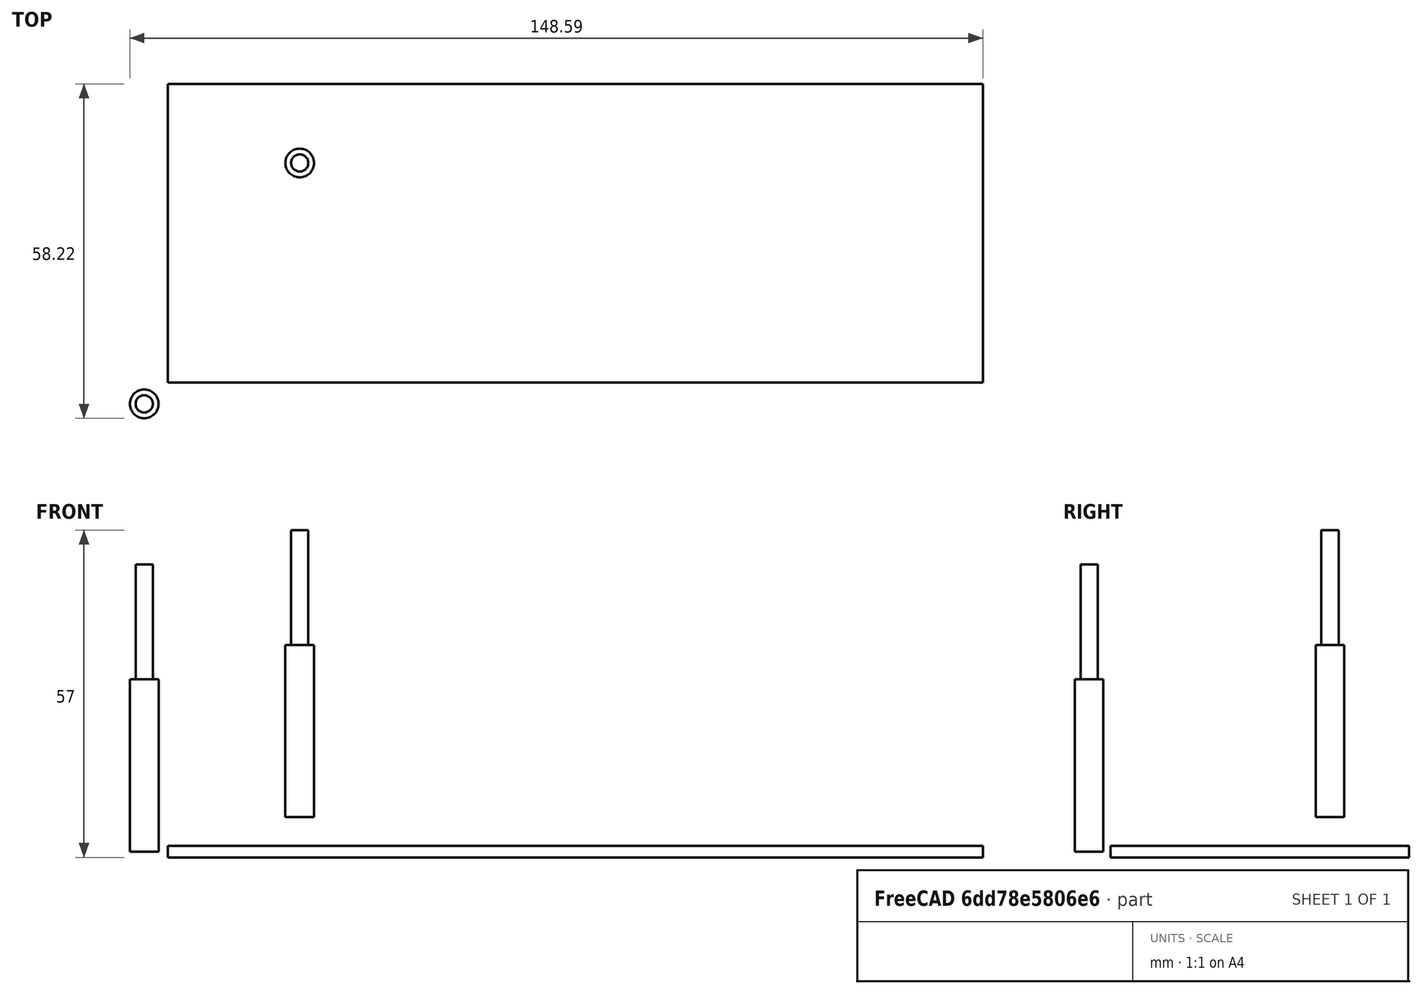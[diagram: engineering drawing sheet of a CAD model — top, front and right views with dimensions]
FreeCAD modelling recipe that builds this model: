
FCSTD DOCUMENT  (FreeCAD 1.0R39109 (Git))
Label: Sensors
License: All rights reserved
LicenseURL: https://en.wikipedia.org/wiki/All_rights_reserved
objects: Sketcher::SketchObject×6, App::DocumentObjectGroup×3, Part::FeaturePython×3, Path::FeaturePython×3, PartDesign::Body×1, App::FeaturePython×1, Part::Part2DObjectPython×1, Mesh::FeaturePython×1
note: 17 computed .brp shape members not serialized (recipe doc carries the construction recipe); baked Part::Feature solids carry a one-line shape summary decoded from their .brp

FEATURE [Sketcher::SketchObject] Sketch004
  ArcFitTolerance = 1e-06
  AttachmentSupport = -> [XY_Plane]
  FullyConstrained = false
  MakeInternals = false
  MapMode = 5
  sketch-geometry (28):
    g0: LineSegment StartX=5.18436 StartY=54.9008 StartZ=0 EndX=5.18436 EndY=4.90076 EndZ=0
    g1: LineSegment StartX=5.18436 StartY=4.90076 StartZ=0 EndX=145.184 EndY=4.90076 EndZ=0
    g2: LineSegment StartX=145.184 StartY=54.9008 StartZ=0 EndX=5.18436 EndY=54.9008 EndZ=0
    g3: LineSegment StartX=145.184 StartY=4.90076 StartZ=0 EndX=145.184 EndY=29.9008 EndZ=0
    g4: LineSegment StartX=145.184 StartY=29.9008 StartZ=0 EndX=145.184 EndY=54.9008 EndZ=0
    g5: LineSegment [constr] StartX=145.184 StartY=29.9008 StartZ=0 EndX=5.18436 EndY=29.9008 EndZ=0
    g6: LineSegment StartX=128.684 StartY=29.9008 StartZ=0 EndX=128.684 EndY=37.4008 EndZ=0
    g7: LineSegment StartX=128.684 StartY=37.4008 StartZ=0 EndX=121.684 EndY=37.4008 EndZ=0
    g8: LineSegment StartX=121.684 StartY=37.4008 StartZ=0 EndX=121.684 EndY=22.4008 EndZ=0
    g9: LineSegment StartX=128.684 StartY=22.4008 StartZ=0 EndX=128.684 EndY=29.9008 EndZ=0
    g10: LineSegment StartX=121.684 StartY=22.4008 StartZ=0 EndX=125.184 EndY=22.4008 EndZ=0
    g11: LineSegment StartX=125.184 StartY=22.4008 StartZ=0 EndX=128.684 EndY=22.4008 EndZ=0
    g12: LineSegment [constr] StartX=125.184 StartY=40.4008 StartZ=0 EndX=125.184 EndY=29.9008 EndZ=0
    g13: LineSegment [constr] StartX=125.184 StartY=29.9008 StartZ=0 EndX=125.184 EndY=19.4008 EndZ=0
    g14: Circle CenterX=125.184 CenterY=19.4008 CenterZ=0 NormalX=0 NormalY=0 NormalZ=1 AngleXU=0 Radius=2
    g15: Circle CenterX=125.184 CenterY=40.4008 CenterZ=0 NormalX=0 NormalY=0 NormalZ=1 AngleXU=0 Radius=2
    g16: LineSegment StartX=28.6844 StartY=29.9008 StartZ=0 EndX=28.6844 EndY=37.4008 EndZ=0
    g17: LineSegment StartX=28.6844 StartY=37.4008 StartZ=0 EndX=21.6844 EndY=37.4008 EndZ=0
    g18: LineSegment StartX=21.6844 StartY=37.4008 StartZ=0 EndX=21.6844 EndY=22.4008 EndZ=0
    g19: LineSegment StartX=28.6844 StartY=22.4008 StartZ=0 EndX=28.6844 EndY=29.9008 EndZ=0
    g20: LineSegment StartX=21.6844 StartY=22.4008 StartZ=0 EndX=25.1844 EndY=22.4008 EndZ=0
    g21: LineSegment StartX=25.1844 StartY=22.4008 StartZ=0 EndX=28.6844 EndY=22.4008 EndZ=0
    g22: LineSegment [constr] StartX=25.1844 StartY=40.4008 StartZ=0 EndX=25.1844 EndY=29.9008 EndZ=0
    g23: LineSegment [constr] StartX=25.1844 StartY=29.9008 StartZ=0 EndX=25.1844 EndY=19.4008 EndZ=0
    g24: Circle CenterX=25.1844 CenterY=19.4008 CenterZ=0 NormalX=0 NormalY=0 NormalZ=1 AngleXU=0 Radius=2
    g25: Circle CenterX=25.1844 CenterY=40.4008 CenterZ=0 NormalX=0 NormalY=0 NormalZ=1 AngleXU=0 Radius=2
    g26: LineSegment [constr] StartX=25.1844 StartY=19.4008 StartZ=0 EndX=125.184 EndY=19.4008 EndZ=0
    g27: LineSegment [constr] StartX=25.1844 StartY=40.4008 StartZ=0 EndX=125.184 EndY=40.4008 EndZ=0
  constraints (78):
    c: Coincident(g0,g1)
    c: Coincident(g2,g0)
    c: Vertical(g0)
    c: Horizontal(g1)
    c: Horizontal(g2)
    c: DistanceX(g2,g2) = 140
    c: DistanceY(g1,g2) = 50
    c: Coincident(g3,g1)
    c: Vertical(g3)
    c: Coincident(g4,g3)
    c: Coincident(g4,g2)
    c: Vertical(g4)
    c: Equal(g3,g4)
    c: Coincident(g5,g3)
    c: PointOnObject(g5,g0)
    c: Horizontal(g5)
    c: PointOnObject(g6,g5)
    c: Vertical(g6)
    c: Coincident(g7,g6)
    c: Horizontal(g7)
    c: Coincident(g8,g7)
    c: Vertical(g8)
    c: Coincident(g9,g6)
    c: Vertical(g9)
    c: Equal(g9,g6)
    c: DistanceX(g7,g7) = 7
    c: DistanceY(g8,g8) = 15
    c: Coincident(g10,g8)
    c: Horizontal(g10)
    c: Coincident(g11,g10)
    c: Coincident(g11,g9)
    c: Horizontal(g11)
    c: Equal(g10,g11)
    c: PointOnObject(g12,g5)
    c: Vertical(g12)
    c: Coincident(g13,g12)
    c: Vertical(g13)
    c: PointOnObject(g10,g13)
    c: Equal(g12,g13)
    c: Coincident(g14,g13)
    c: Coincident(g15,g12)
    c: Diameter(g15) = 4
    c: Equal(g14,g15)
    c: Vertical(g16)
    c: Coincident(g17,g16)
    c: Horizontal(g17)
    c: Coincident(g18,g17)
    c: Vertical(g18)
    c: Coincident(g19,g16)
    c: Vertical(g19)
    c: Equal(g19,g16)
    c: DistanceX(g17,g17) = 7
    c: DistanceY(g18,g18) = 15
    c: Coincident(g20,g18)
    c: Horizontal(g20)
    c: Coincident(g21,g20)
    c: Coincident(g21,g19)
    c: Horizontal(g21)
    c: Equal(g20,g21)
    c: Vertical(g22)
    c: Coincident(g23,g22)
    c: Vertical(g23)
    c: PointOnObject(g20,g23)
    c: Equal(g22,g23)
    c: Coincident(g24,g23)
    c: Coincident(g25,g22)
    c: Diameter(g25) = 4
    c: Equal(g24,g25)
    c: DistanceX(g0,g22) = 20
    c: DistanceX(g19,g9) = 100
    c: PointOnObject(g16,g5)
    c: Coincident(g26,g23)
    c: Coincident(g26,g13)
    c: Horizontal(g26)
    c: Coincident(g27,g22)
    c: Coincident(g27,g12)
    c: Horizontal(g27)
    c: DistanceY(g13,g12) = 21
FEATURE [Sketcher::SketchObject] Sketch001  label="Frame001"
  ArcFitTolerance = 1e-06
  AttachmentSupport = -> [XY_Plane]
  FullyConstrained = false
  MakeInternals = false
  MapMode = 5
  sketch-geometry (13):
    g0: LineSegment StartX=42.7516 StartY=74.1544 StartZ=0 EndX=42.7516 EndY=39.1544 EndZ=0
    g1: LineSegment StartX=42.7516 StartY=39.1544 StartZ=0 EndX=82.7516 EndY=39.1544 EndZ=0
    g2: LineSegment StartX=82.7516 StartY=39.1544 StartZ=0 EndX=82.7516 EndY=74.1544 EndZ=0
    g3: LineSegment StartX=82.7516 StartY=74.1544 StartZ=0 EndX=42.7516 EndY=74.1544 EndZ=0
    g4: LineSegment StartX=42.7516 StartY=74.1544 StartZ=0 EndX=7.75162 EndY=39.1544 EndZ=0
    g5: LineSegment StartX=7.75162 StartY=39.1544 StartZ=0 EndX=42.7516 EndY=39.1544 EndZ=0
    g6: LineSegment StartX=82.7516 StartY=39.1544 StartZ=0 EndX=117.752 EndY=39.1544 EndZ=0
    g7: LineSegment StartX=117.752 StartY=39.1544 StartZ=0 EndX=82.7516 EndY=74.1544 EndZ=0
    g8: LineSegment StartX=42.7516 StartY=39.1544 StartZ=0 EndX=42.7516 EndY=4.15437 EndZ=0
    g9: LineSegment StartX=42.7516 StartY=4.15437 StartZ=0 EndX=82.7516 EndY=4.15437 EndZ=0
    g10: LineSegment StartX=82.7516 StartY=4.15437 StartZ=0 EndX=82.7516 EndY=39.1544 EndZ=0
    g11: Circle CenterX=7.75162 CenterY=4.15437 CenterZ=0 NormalX=0 NormalY=0 NormalZ=1 AngleXU=0 Radius=2.75
    g12: Circle CenterX=7.75162 CenterY=74.1544 CenterZ=0 NormalX=0 NormalY=0 NormalZ=1 AngleXU=0 Radius=2.8
  constraints (34):
    c: Coincident(g0,g1)
    c: Coincident(g1,g2)
    c: Coincident(g2,g3)
    c: Coincident(g3,g0)
    c: Vertical(g0)
    c: Vertical(g2)
    c: Horizontal(g1)
    c: Horizontal(g3)
    c: DistanceX(g3,g3) = 40
    c: DistanceY(g2,g2) = 35
    c: Coincident(g4,g0)
    c: Coincident(g5,g4)
    c: Coincident(g5,g0)
    c: Horizontal(g5)
    c: Coincident(g6,g1)
    c: Coincident(g7,g6)
    c: Coincident(g7,g2)
    c: Horizontal(g6)
    c: Coincident(g8,g0)
    c: Vertical(g8)
    c: Coincident(g9,g8)
    c: Horizontal(g9)
    c: Coincident(g10,g9)
    c: Coincident(g10,g1)
    c: Vertical(g10)
    c: DistanceX(g5,g5) = 35
    c: Equal(g5,g6)
    c: Equal(g6,g10)
    c: Diameter(g11) = 5.5
    c: Horizontal(g11,g8)
    c: Vertical(g11,g4)
    c: Diameter(g12) = 5.6
    c: Vertical(g4,g12)
    c: Horizontal(g12,g0)
FEATURE [Sketcher::SketchObject] Sketch002  label="Bracket002"
  ArcFitTolerance = 1e-06
  AttachmentSupport = -> [XY_Plane]
  ExternalGeometry = -> [Sketch001]
  FullyConstrained = false
  MakeInternals = false
  MapMode = 5
  sketch-geometry (42):
    g0: LineSegment StartX=42.7516 StartY=74.1544 StartZ=0 EndX=42.7516 EndY=64.7012 EndZ=0
    g1: LineSegment StartX=42.7516 StartY=64.7012 StartZ=0 EndX=46.7516 EndY=64.7012 EndZ=0
    g2: LineSegment StartX=46.7516 StartY=64.7012 StartZ=0 EndX=46.7516 EndY=50.9202 EndZ=0
    g3: LineSegment StartX=46.7516 StartY=50.9202 StartZ=0 EndX=42.7516 EndY=50.9202 EndZ=0
    g4: LineSegment StartX=42.7516 StartY=50.9202 StartZ=0 EndX=42.7516 EndY=39.1544 EndZ=0
    g5: LineSegment StartX=42.7516 StartY=39.1544 StartZ=0 EndX=46.7516 EndY=39.1544 EndZ=0
    g6: LineSegment StartX=46.7516 StartY=39.1544 StartZ=0 EndX=46.7516 EndY=35.1544 EndZ=0
    g7: LineSegment StartX=78.7516 StartY=35.1544 StartZ=0 EndX=78.7516 EndY=39.1544 EndZ=0
    g8: LineSegment StartX=78.7516 StartY=39.1544 StartZ=0 EndX=82.7516 EndY=39.1544 EndZ=0
    g9: LineSegment StartX=82.7516 StartY=39.1544 StartZ=0 EndX=82.7516 EndY=49.7839 EndZ=0
    g10: LineSegment StartX=82.7516 StartY=49.7839 StartZ=0 EndX=78.7516 EndY=49.7839 EndZ=0
    g11: LineSegment StartX=78.7516 StartY=49.7839 StartZ=0 EndX=78.7516 EndY=63.8113 EndZ=0
    g12: LineSegment StartX=78.7516 StartY=63.8113 StartZ=0 EndX=82.7516 EndY=63.8113 EndZ=0
    g13: LineSegment StartX=82.7516 StartY=63.8113 StartZ=0 EndX=82.7516 EndY=74.1544 EndZ=0
    g14: LineSegment StartX=82.7516 StartY=74.1544 StartZ=0 EndX=42.7516 EndY=74.1544 EndZ=0
    g15: LineSegment StartX=42.7516 StartY=74.1544 StartZ=0 EndX=42.7516 EndY=64.7012 EndZ=0
    g16: LineSegment StartX=42.7516 StartY=25.1544 StartZ=0 EndX=46.91 EndY=25.1544 EndZ=0
    g17: LineSegment StartX=46.91 StartY=25.1544 StartZ=0 EndX=46.91 EndY=4.15437 EndZ=0
    g18: LineSegment StartX=46.7516 StartY=35.1544 StartZ=0 EndX=78.7516 EndY=35.1544 EndZ=0
    g19: LineSegment [constr] StartX=46.7516 StartY=39.1544 StartZ=0 EndX=46.7516 EndY=50.9202 EndZ=0
    g20: LineSegment [constr] StartX=78.7516 StartY=39.1544 StartZ=0 EndX=78.7516 EndY=49.7839 EndZ=0
    g21: LineSegment StartX=42.7516 StartY=25.1544 StartZ=0 EndX=42.7516 EndY=39.1544 EndZ=0
    g22: LineSegment StartX=28.7516 StartY=39.1544 StartZ=0 EndX=28.7516 EndY=35.1544 EndZ=0
    g23: LineSegment StartX=28.7516 StartY=35.1544 StartZ=0 EndX=7.75162 EndY=35.1544 EndZ=0
    g24: LineSegment StartX=7.75162 StartY=35.1544 StartZ=0 EndX=7.75162 EndY=39.1544 EndZ=0
    g25: LineSegment StartX=42.7516 StartY=39.1544 StartZ=0 EndX=38.7516 EndY=39.1544 EndZ=0
    g26: LineSegment StartX=38.7516 StartY=39.1544 StartZ=0 EndX=28.7516 EndY=39.1544 EndZ=0
    g27: LineSegment StartX=7.75162 StartY=39.1544 StartZ=0 EndX=42.7516 EndY=74.1544 EndZ=0
    g28: LineSegment StartX=82.7516 StartY=39.1544 StartZ=0 EndX=87.4455 EndY=39.1544 EndZ=0
    g29: LineSegment StartX=87.4455 StartY=39.1544 StartZ=0 EndX=96.7516 EndY=39.1544 EndZ=0
    g30: LineSegment StartX=96.7516 StartY=39.1544 StartZ=0 EndX=96.7516 EndY=35.1544 EndZ=0
    g31: LineSegment StartX=96.7516 StartY=35.1544 StartZ=0 EndX=117.752 EndY=35.1544 EndZ=0
    g32: LineSegment StartX=117.752 StartY=35.1544 StartZ=0 EndX=117.752 EndY=39.1544 EndZ=0
    g33: LineSegment StartX=117.752 StartY=39.1544 StartZ=0 EndX=82.7516 EndY=74.1544 EndZ=0
    g34: LineSegment [constr] StartX=96.7516 StartY=35.1544 StartZ=0 EndX=78.7516 EndY=35.1544 EndZ=0
    g35: LineSegment [constr] StartX=46.7516 StartY=35.1544 StartZ=0 EndX=28.7516 EndY=35.1544 EndZ=0
    g36: LineSegment StartX=82.7516 StartY=39.1544 StartZ=0 EndX=82.7516 EndY=25.2722 EndZ=0
    g37: LineSegment StartX=82.7516 StartY=25.2722 StartZ=0 EndX=78.7516 EndY=25.2722 EndZ=0
    g38: LineSegment StartX=78.7516 StartY=25.2722 StartZ=0 EndX=78.7516 EndY=4.15437 EndZ=0
    g39: LineSegment StartX=78.7516 StartY=4.15437 StartZ=0 EndX=46.91 EndY=4.15437 EndZ=0
    g40: LineSegment [constr] StartX=46.7516 StartY=25.1544 StartZ=0 EndX=46.7516 EndY=35.1544 EndZ=0
    g41: LineSegment [constr] StartX=78.7516 StartY=25.2722 StartZ=0 EndX=78.7516 EndY=35.1544 EndZ=0
  constraints (109):
    c: Coincident(g0,g-3)
    c: PointOnObject(g0,g-3)
    c: Coincident(g1,g0)
    c: Horizontal(g1)
    c: Coincident(g2,g1)
    c: Vertical(g2)
    c: Coincident(g3,g2)
    c: PointOnObject(g3,g-3)
    c: Horizontal(g3)
    c: Coincident(g4,g3)
    c: Horizontal(g5)
    c: Coincident(g6,g5)
    c: Vertical(g6)
    c: DistanceX(g1,g1) = 4
    c: Distance(g7) = 4
    c: Vertical(g7)
    c: Coincident(g8,g7)
    c: PointOnObject(g8,g-7)
    c: Horizontal(g8)
    c: Coincident(g9,g8)
    c: PointOnObject(g9,g-7)
    c: Coincident(g10,g9)
    c: Horizontal(g10)
    c: Coincident(g11,g10)
    c: Vertical(g11)
    c: Coincident(g12,g11)
    c: PointOnObject(g12,g-7)
    c: Horizontal(g12)
    c: Coincident(g13,g12)
    c: Coincident(g13,g-7)
    c: Coincident(g14,g13)
    c: Coincident(g14,g0)
    c: Coincident(g15,g0)
    c: Coincident(g15,g0)
    c: Horizontal(g16)
    c: Coincident(g17,g16)
    c: Vertical(g17)
    c: PointOnObject(g17,g-13)
    c: DistanceX(g12,g12) = 4
    c: DistanceX(g1,g1) = 4
    c: Coincident(g18,g6)
    c: Coincident(g18,g7)
    c: Horizontal(g18)
    c: Coincident(g19,g5)
    c: Coincident(g19,g2)
    c: Vertical(g19)
    c: Coincident(g20,g7)
    c: Coincident(g20,g10)
    c: Vertical(g20)
    c: Coincident(g4,g-5)
    c: Coincident(g5,g4)
    c: Coincident(g21,g16)
    c: Coincident(g21,g4)
    c: Vertical(g21)
    c: Vertical(g22)
    c: Coincident(g23,g22)
    c: Horizontal(g23)
    c: Coincident(g24,g23)
    c: Coincident(g24,g-11)
    c: Vertical(g24)
    c: Coincident(g25,g4)
    c: PointOnObject(g25,g-4)
    c: Coincident(g26,g25)
    c: Coincident(g26,g22)
    c: Horizontal(g26)
    c: Equal(g25,g5)
    c: DistanceX(g25,g25) = 4
    c: DistanceX(g23,g23) = 21
    c: DistanceY(g17,g17) = 21
    c: DistanceY(g21,g21) = 14
    c: DistanceX(g22,g4) = 14
    c: Coincident(g27,g24)
    c: Coincident(g27,g0)
    c: Coincident(g28,g8)
    c: PointOnObject(g28,g-8)
    c: Coincident(g29,g28)
    c: PointOnObject(g29,g-8)
    c: Coincident(g30,g29)
    c: Vertical(g30)
    c: Coincident(g31,g30)
    c: Horizontal(g31)
    c: Coincident(g32,g31)
    c: Coincident(g32,g-12)
    c: Coincident(g33,g32)
    c: Coincident(g33,g13)
    c: Vertical(g32)
    c: Coincident(g34,g30)
    c: Coincident(g34,g7)
    c: Horizontal(g34)
    c: Coincident(g35,g6)
    c: Coincident(g35,g22)
    c: Horizontal(g35)
    c: DistanceX(g8,g29) = 14
    c: DistanceX(g31,g31) = 21
    c: Coincident(g36,g8)
    c: PointOnObject(g36,g-6)
    c: Coincident(g37,g36)
    c: Horizontal(g37)
    c: Coincident(g38,g37)
    c: PointOnObject(g38,g-13)
    c: Vertical(g38)
    c: Coincident(g39,g38)
    c: Coincident(g39,g17)
    c: Coincident(g41,g37)
    c: Coincident(g41,g7)
    c: Vertical(g41)
    c: Vertical(g40)
    c: Coincident(g40,g6)
    c: PointOnObject(g8,g-8)
FEATURE [Sketcher::SketchObject] Sketch003  label="Sensor003"
  ArcFitTolerance = 1e-06
  AttachmentSupport = -> [XY_Plane]
  ExternalGeometry = -> [Sketch002]
  FullyConstrained = false
  MakeInternals = false
  MapMode = 5
  sketch-geometry (15):
    g0: LineSegment [constr] StartX=42.7516 StartY=74.1544 StartZ=0 EndX=62.7516 EndY=74.1544 EndZ=0
    g1: LineSegment [constr] StartX=62.7516 StartY=74.1544 StartZ=0 EndX=82.7516 EndY=74.1544 EndZ=0
    g2: LineSegment StartX=59.7516 StartY=65.1544 StartZ=0 EndX=59.7516 EndY=50.1544 EndZ=0
    g3: LineSegment StartX=65.7516 StartY=50.1544 StartZ=0 EndX=65.7516 EndY=65.1544 EndZ=0
    g4: LineSegment StartX=65.7516 StartY=65.1544 StartZ=0 EndX=62.7516 EndY=65.1544 EndZ=0
    g5: LineSegment StartX=62.7516 StartY=65.1544 StartZ=0 EndX=59.7516 EndY=65.1544 EndZ=0
    g6: Circle CenterX=62.7516 CenterY=46.6544 CenterZ=0 NormalX=0 NormalY=0 NormalZ=1 AngleXU=0 Radius=1.53845
    g7: Circle CenterX=62.7516 CenterY=68.6544 CenterZ=0 NormalX=0 NormalY=0 NormalZ=1 AngleXU=0 Radius=1.53845
    g8: LineSegment [constr] StartX=62.7516 StartY=74.1544 StartZ=0 EndX=62.7516 EndY=68.6544 EndZ=0
    g9: LineSegment [constr] StartX=62.7516 StartY=68.6544 StartZ=0 EndX=62.7516 EndY=65.1544 EndZ=0
    g10: LineSegment [constr] StartX=62.7516 StartY=50.1544 StartZ=0 EndX=62.7516 EndY=46.6544 EndZ=0
    g11: LineSegment [constr] StartX=62.7516 StartY=65.1544 StartZ=0 EndX=62.7516 EndY=57.6544 EndZ=0
    g12: LineSegment [constr] StartX=62.7516 StartY=57.6544 StartZ=0 EndX=62.7516 EndY=50.1544 EndZ=0
    g13: LineSegment StartX=65.7516 StartY=50.1544 StartZ=0 EndX=62.7516 EndY=50.1544 EndZ=0
    g14: LineSegment StartX=62.7516 StartY=50.1544 StartZ=0 EndX=59.7516 EndY=50.1544 EndZ=0
  constraints (39):
    c: Coincident(g0,g-3)
    c: Coincident(g1,g0)
    c: Coincident(g1,g-3)
    c: Equal(g1,g0)
    c: PointOnObject(g0,g-3)
    c: Vertical(g2)
    c: Vertical(g3)
    c: Coincident(g4,g3)
    c: Horizontal(g4)
    c: Coincident(g5,g4)
    c: Coincident(g5,g2)
    c: Horizontal(g5)
    c: Equal(g4,g5)
    c: DistanceY(g3,g3) = 15
    c: Equal(g6,g7)
    c: Coincident(g8,g0)
    c: Coincident(g8,g7)
    c: Vertical(g8)
    c: Coincident(g9,g7)
    c: Coincident(g9,g4)
    c: Vertical(g9)
    c: Coincident(g10,g6)
    c: Vertical(g10)
    c: Coincident(g11,g4)
    c: Vertical(g11)
    c: Coincident(g12,g11)
    c: Coincident(g12,g10)
    c: Vertical(g12)
    c: Equal(g12,g11)
    c: Coincident(g13,g3)
    c: Coincident(g13,g10)
    c: Coincident(g14,g10)
    c: Coincident(g14,g2)
    c: Horizontal(g14)
    c: Horizontal(g13)
    c: Equal(g10,g9)
    c: DistanceY(g6,g7) = 22
    c: DistanceX(g2,g3) = 6
    c: DistanceY(g-4,g6) = 7.5
FEATURE [Sketcher::SketchObject] Sketch  label="A3"
  ArcFitTolerance = 1e-06
  AttachmentSupport = -> [XY_Plane]
  FullyConstrained = true
  MakeInternals = false
  MapMode = 5
  sketch-geometry (6):
    g0: LineSegment StartX=0 StartY=0 StartZ=0 EndX=420 EndY=0 EndZ=0
    g1: LineSegment StartX=420 StartY=0 StartZ=0 EndX=420 EndY=297 EndZ=0
    g2: LineSegment StartX=0 StartY=297 StartZ=0 EndX=0 EndY=0 EndZ=0
    g3: LineSegment StartX=0 StartY=297 StartZ=0 EndX=210 EndY=297 EndZ=0
    g4: LineSegment StartX=210 StartY=297 StartZ=0 EndX=420 EndY=297 EndZ=0
    g5: LineSegment StartX=210 StartY=297 StartZ=0 EndX=210 EndY=0 EndZ=0
  constraints (16):
    c: Coincident(g0,g1)
    c: Coincident(g2,g0)
    c: Horizontal(g0)
    c: Vertical(g1)
    c: Vertical(g2)
    c: Coincident(g0,g-1)
    c: DistanceX(g2,g1) = 420
    c: DistanceY(g2,g2) = 297
    c: Coincident(g3,g2)
    c: Horizontal(g3)
    c: Coincident(g4,g3)
    c: Coincident(g4,g1)
    c: Horizontal(g4)
    c: Equal(g4,g3)
    c: Coincident(g5,g3)
    c: Symmetric(g0,g0,g5)
FEATURE [PartDesign::Body] Body
  AllowCompound = false
  Group = -> [Sketch,Sketch001,Sketch002,Sketch003]
  Origin = -> Origin
FEATURE [Sketcher::SketchObject] Sketch005  label="DUMMY"
  ArcFitTolerance = 1e-06
  AttachmentSupport = -> [Sketch004]
  FullyConstrained = true
  MakeInternals = false
  MapMode = 2
FEATURE [App::FeaturePython] SetupSheet  # Path/CAM operation (typed FeaturePython)
  ClearanceHeightExpression = OpStockZMax+SetupSheet.ClearanceHeightOffset
  ClearanceHeightOffset = 5
  CoolantMode = 0
  CoolantModes = None | Flood | Mist
  FinalDepthExpression = OpFinalDepth
  HorizRapid = 0
  SafeHeightExpression = OpStockZMax+SetupSheet.SafeHeightOffset
  SafeHeightOffset = 3
  StartDepthExpression = OpStartDepth
  StepDownExpression = OpToolDiameter
  VertRapid = 0
FEATURE [Part::Part2DObjectPython] Clone2D  label="Model-Sketch004"  # Draft 2D object (typed FeaturePython)
  Fuse = false
  Objects = -> [Sketch004]
  PathResource = Model
  Scale = (1,1,1)
FEATURE [App::DocumentObjectGroup] Model
  Group = -> [Clone2D]
FEATURE [Part::FeaturePython] ToolBit  label="Endmill"  # Path/CAM toolbit (typed FeaturePython)
  BitPropertyNames = Chipload | CuttingEdgeHeight | Diameter | Flutes | Length | Material | ShankDiameter | SpindleDirection
  BitShape = <path>
  Chipload = 0
  CuttingEdgeHeight = 30
  Diameter = 5
  Flutes = 0
  Length = 50
  Material = 0
  ShankDiameter = 3
  ShapeName = endmill
  SpindleDirection = 0
FEATURE [Path::FeaturePython] TC__Default_Tool  label="TC: Default Tool"  # Path/CAM operation (typed FeaturePython)
  HorizFeed = 1000
  HorizRapid = 1000
  SpindleDir = 1
  SpindleSpeed = 1000
  Tool = -> ToolBit
  ToolNumber = 1
  VertFeed = 1000
  VertRapid = 1000
  expr: HorizFeed = 1000
  expr: HorizRapid = 1000
  expr: VertFeed = 1000
  expr: VertRapid = 1000
FEATURE [App::DocumentObjectGroup] Tools
  Group = -> [TC__Default_Tool]
FEATURE [Part::FeaturePython] Stock  # WARN: FeaturePython — macro-defined, semantics opaque (R4)
  Base = -> Model
  ExtXneg = 1
  ExtXpos = 1
  ExtYneg = 1
  ExtYpos = 1
  ExtZneg = 1
  ExtZpos = 1
  Placement = pos=(5.08792,4.71701,0) rot=(0,0,1;0rad)
  StockType = FromBase
FEATURE [Path::FeaturePython] Engrave  # Path/CAM operation (typed FeaturePython)
  Active = true
  ClearanceHeight = 6
  CoolantMode = 0
  CycleTime = 00:00:00
  FinalDepth = -5
  OpFinalDepth = -5
  OpStartDepth = 0
  OpStockZMax = 1
  OpStockZMin = -1
  OpToolDiameter = 5
  SafeHeight = 4
  StartDepth = 0
  StartVertex = 0
  StepDown = 5
  ToolController = -> TC__Default_Tool
  expr: ClearanceHeight = OpStockZMax + SetupSheet.ClearanceHeightOffset
  expr: FinalDepth = OpFinalDepth
  expr: SafeHeight = OpStockZMax + SetupSheet.SafeHeightOffset
  expr: StartDepth = OpStartDepth
  expr: StepDown = OpToolDiameter
FEATURE [App::DocumentObjectGroup] Operations
  Group = -> [Engrave]
FEATURE [Path::FeaturePython] Job  # Path/CAM operation (typed FeaturePython)
  CycleTime = 00:00:00
  Fixtures = G54
  GeometryTolerance = 0.01
  JobType = 0
  Model = -> Model
  Operations = -> Operations
  OrderOutputBy = 0
  PostProcessor = 1
  SetupSheet = -> SetupSheet
  SplitOutput = false
  Stock = -> Stock
  Tools = -> Tools
FEATURE [Part::FeaturePython] CutTool  # WARN: FeaturePython — macro-defined, semantics opaque (R4)
  Placement = pos=(27.0879,41.9607,6) rot=(0,0,1;0rad)
FEATURE [Mesh::FeaturePython] CutMaterial  # WARN: FeaturePython — macro-defined, semantics opaque (R4)
note: 1 file-system path scrubbed to <path> (originals preserved in the JSON sidecar)
